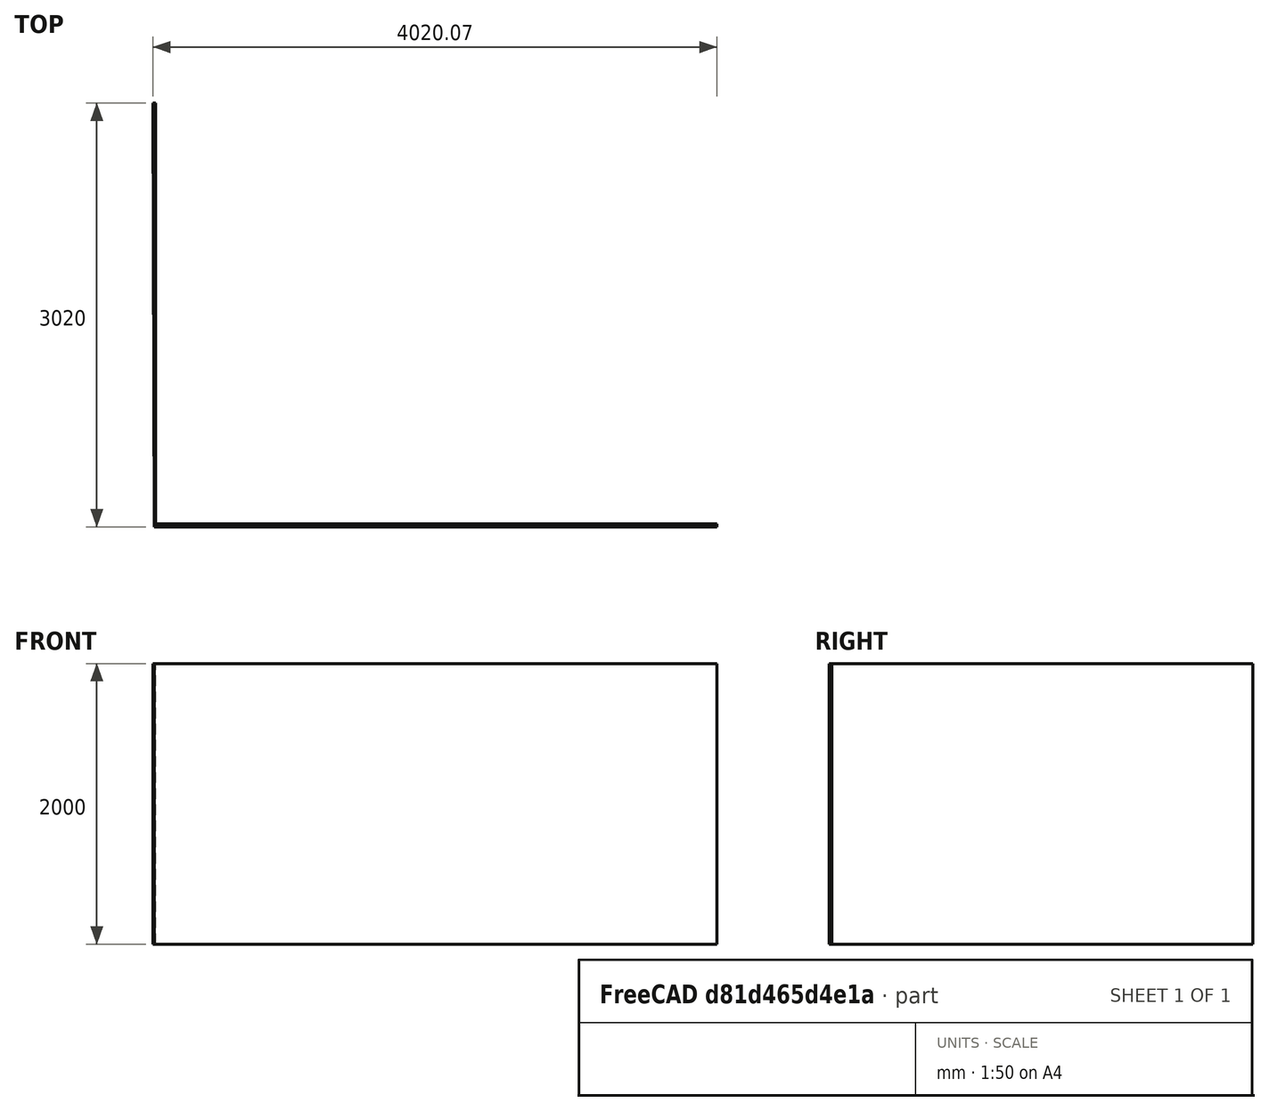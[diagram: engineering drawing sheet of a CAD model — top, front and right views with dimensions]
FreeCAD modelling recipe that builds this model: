
FCSTD DOCUMENT  (FreeCAD 0.15R4606 (Git))
Label: cell4
License: All rights reserved
LicenseURL: http://en.wikipedia.org/wiki/All_rights_reserved
objects: Sketcher::SketchObject×1, PartDesign::Pad×1
note: 3 computed .brp shape members not serialized (recipe doc carries the construction recipe); baked Part::Feature solids carry a one-line shape summary decoded from their .brp

FEATURE [Sketcher::SketchObject] Sketch
  sketch-geometry (6):
    g0: LineSegment StartX=-1520 StartY=1500 StartZ=0 EndX=-1500 EndY=1500 EndZ=0
    g1: LineSegment StartX=-1500 StartY=1500 StartZ=0 EndX=-1500 EndY=-1500 EndZ=0
    g2: LineSegment StartX=-1500 StartY=-1500 StartZ=0 EndX=2500 EndY=-1500 EndZ=0
    g3: LineSegment StartX=2500 StartY=-1500 StartZ=0 EndX=2500.07 EndY=-1520 EndZ=0
    g4: LineSegment StartX=2500.07 StartY=-1520 StartZ=0 EndX=-1510 EndY=-1520 EndZ=0
    g5: LineSegment StartX=-1510 StartY=-1520 StartZ=0 EndX=-1520 EndY=1500 EndZ=0
  constraints (18):
    c: Horizontal(g0)
    c: Coincident(g0,g1)
    c: Vertical(g1)
    c: Coincident(g1,g2)
    c: Horizontal(g2)
    c: Coincident(g2,g3)
    c: Coincident(g3,g4)
    c: Horizontal(g4)
    c: Coincident(g4,g5)
    c: Coincident(g5,g0)
    c: DistanceX(g0) = 20
    c: DistanceY(g3) = -20
    c: DistanceY(g1) = -3000
    c: DistanceX(g2) = 4000
    c: Distance(g-1,g2) = 1500
    c: Distance(g-1,g1) = 1500
    c: Distance(g4,g1) = 10
    c: Parallel(g3,g5)
FEATURE [PartDesign::Pad] Pad  label="wall"
  Length = 2000
  Length2 = 100
  Sketch = -> Sketch
  Type = 0
